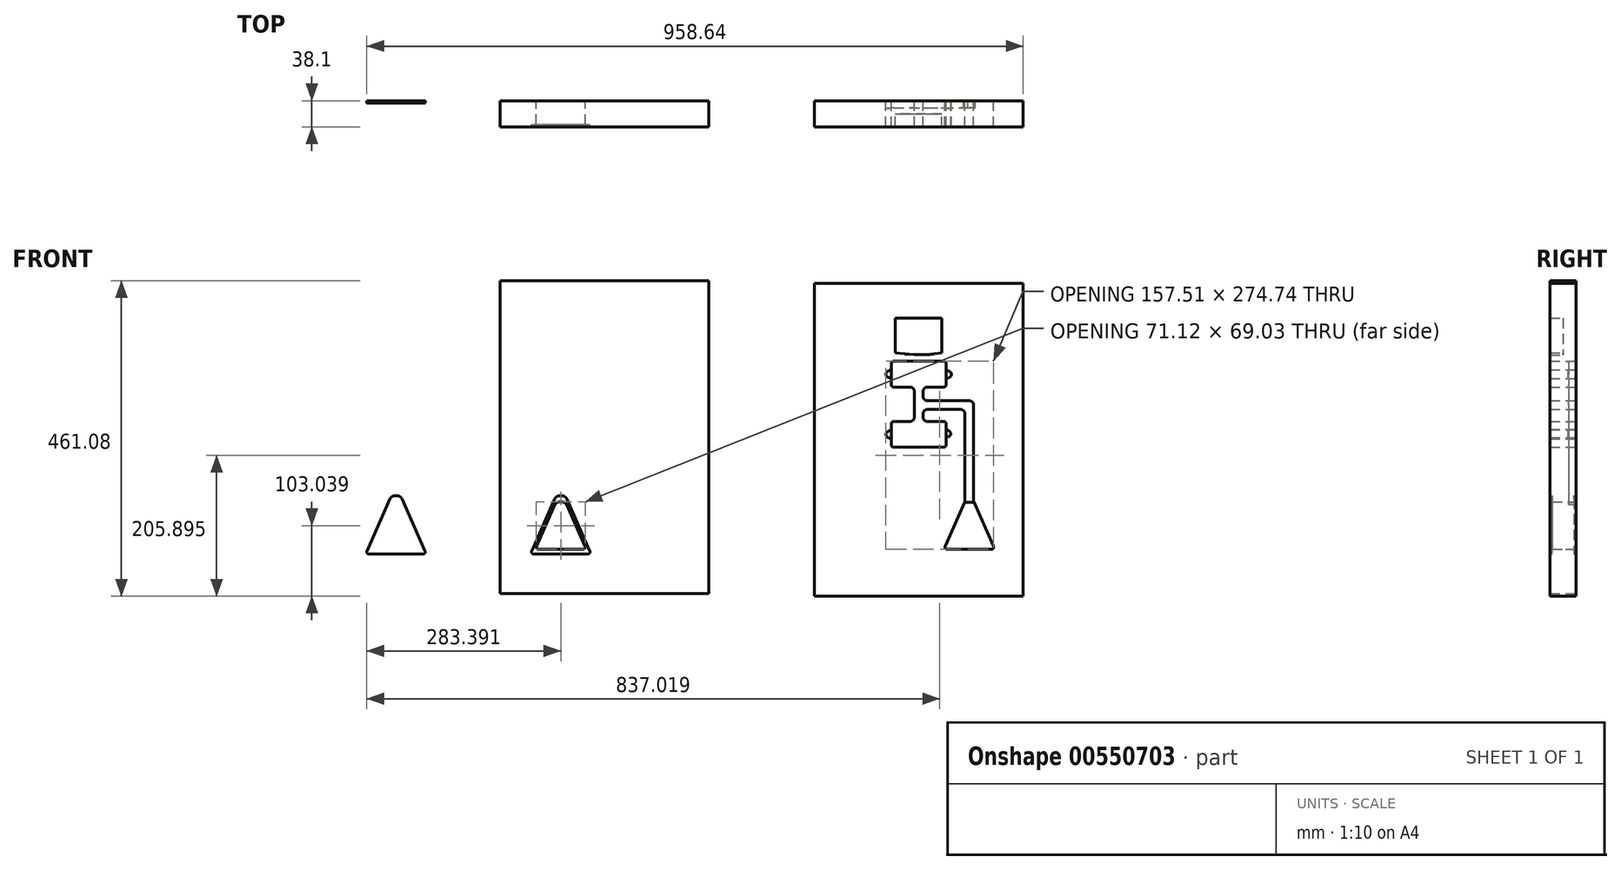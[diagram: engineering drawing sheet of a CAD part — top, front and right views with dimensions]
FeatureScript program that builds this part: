
annotation { "Feature Type Name" : "Feature", "Feature Type Description" : "" }
export const myFeature = defineFeature(function(context is Context, id is Id, definition is map)
    precondition{}
    {
        {
            var Q0;
            Q0=qCreatedBy(makeId("Front.planeOp"),FACE);
            var sketch = newSketch(context, id + "F0", { "sketchPlane" : qUnion([Q0])});
            skLineSegment(sketch, "E0.top", {"start": v(-152.36, -197.5) * mm, "end": v(152.44, -197.5) * mm});
            skLineSegment(sketch, "E0.left", {"start": v(-152.36, 208.9) * mm, "end": v(-152.36, -197.5) * mm});
            skLineSegment(sketch, "E0.right", {"start": v(152.44, 208.9) * mm, "end": v(152.44, -197.5) * mm});
            skLineSegment(sketch, "E1", {"start": v(-33.96, 208.9) * mm, "end": v(-33.96, 158.1) * mm});
            skLineSegment(sketch, "E2", {"start": v(34.04, 208.9) * mm, "end": v(34.04, 158.1) * mm});
            skLineSegment(sketch, "E3", {"start": v(0.04, 208.9) * mm, "end": v(0.04, -197.5) * mm, "construction": true});
            skLineSegment(sketch, "E4", {"start": v(-33.96, 158.1) * mm, "end": v(34.04, 158.1) * mm});
            skLineSegment(sketch, "E5.bottom", {"start": v(-36.8, 57.8) * mm, "end": v(-12.66, 57.8) * mm});
            skLineSegment(sketch, "E5.top", {"start": v(-36.8, 20.2) * mm, "end": v(36.87, 20.2) * mm});
            skLineSegment(sketch, "E5.left", {"start": v(-39.84, 54.75) * mm, "end": v(-39.84, 23.25) * mm});
            skLineSegment(sketch, "E5.right", {"start": v(39.92, 54.75) * mm, "end": v(39.92, 23.25) * mm});
            skLineSegment(sketch, "E6.bottom", {"start": v(-36.8, 145.75) * mm, "end": v(36.87, 145.75) * mm});
            skLineSegment(sketch, "E6.top", {"start": v(-36.8, 108.16) * mm, "end": v(-12.66, 108.16) * mm});
            skLineSegment(sketch, "E6.left", {"start": v(-39.84, 142.7) * mm, "end": v(-39.84, 111.2) * mm});
            skLineSegment(sketch, "E6.right", {"start": v(39.92, 142.7) * mm, "end": v(39.92, 111.2) * mm});
            skPoint(sketch, "E7.visualSharp", {"position": v(-39.84, 57.8) * mm});
            skArc(sketch, "E7.filletArc", {"start": v(-36.8, 57.8) * mm, "mid": v(-38.95, 56.9) * mm, "end": v(-39.84, 54.75) * mm});
            skPoint(sketch, "E8.visualSharp", {"position": v(39.92, 57.8) * mm});
            skArc(sketch, "E8.filletArc", {"start": v(39.92, 54.75) * mm, "mid": v(39.02, 56.9) * mm, "end": v(36.87, 57.8) * mm});
            skPoint(sketch, "E9.visualSharp", {"position": v(39.92, 20.2) * mm});
            skArc(sketch, "E9.filletArc", {"start": v(36.87, 20.2) * mm, "mid": v(39.02, 21.1) * mm, "end": v(39.92, 23.25) * mm});
            skPoint(sketch, "E10.visualSharp", {"position": v(-39.84, 20.2) * mm});
            skArc(sketch, "E10.filletArc", {"start": v(-39.84, 23.25) * mm, "mid": v(-38.95, 21.1) * mm, "end": v(-36.8, 20.2) * mm});
            skPoint(sketch, "E11.visualSharp", {"position": v(-39.84, 145.75) * mm});
            skArc(sketch, "E11.filletArc", {"start": v(-36.8, 145.75) * mm, "mid": v(-38.95, 144.86) * mm, "end": v(-39.84, 142.7) * mm});
            skPoint(sketch, "E12.visualSharp", {"position": v(39.92, 145.75) * mm});
            skArc(sketch, "E12.filletArc", {"start": v(39.92, 142.7) * mm, "mid": v(39.02, 144.86) * mm, "end": v(36.87, 145.75) * mm});
            skPoint(sketch, "E13.visualSharp", {"position": v(39.92, 108.16) * mm});
            skArc(sketch, "E13.filletArc", {"start": v(36.87, 108.16) * mm, "mid": v(39.02, 109.05) * mm, "end": v(39.92, 111.2) * mm});
            skPoint(sketch, "E14.visualSharp", {"position": v(-39.84, 108.16) * mm});
            skArc(sketch, "E14.filletArc", {"start": v(-39.84, 111.2) * mm, "mid": v(-38.95, 109.05) * mm, "end": v(-36.8, 108.16) * mm});
            skLineSegment(sketch, "E15", {"start": v(12.74, 88.05) * mm, "end": v(74.01, 88.05) * mm});
            skLineSegment(sketch, "E16", {"start": v(12.74, 75.35) * mm, "end": v(61.31, 75.35) * mm});
            skLineSegment(sketch, "E17", {"start": v(67.66, 69) * mm, "end": v(67.66, -58.67) * mm});
            skLineSegment(sketch, "E18", {"start": v(80.36, 81.7) * mm, "end": v(80.36, -58.67) * mm});
            skPoint(sketch, "E19.visualSharp", {"position": v(80.36, 88.05) * mm});
            skArc(sketch, "E19.filletArc", {"start": v(80.36, 81.7) * mm, "mid": v(78.5, 86.19) * mm, "end": v(74.01, 88.05) * mm});
            skPoint(sketch, "E20.visualSharp", {"position": v(67.66, 75.35) * mm});
            skArc(sketch, "E20.filletArc", {"start": v(67.66, 69) * mm, "mid": v(65.8, 73.49) * mm, "end": v(61.31, 75.35) * mm});
            skLineSegment(sketch, "E21", {"start": v(6.39, 101.81) * mm, "end": v(6.39, 94.4) * mm});
            skLineSegment(sketch, "E22", {"start": v(-6.31, 101.81) * mm, "end": v(-6.31, 64.15) * mm});
            skLineSegment(sketch, "E23.trimOffspring", {"start": v(6.39, 69) * mm, "end": v(6.39, 64.15) * mm});
            skLineSegment(sketch, "E24.trimOffspring", {"start": v(12.74, 108.16) * mm, "end": v(36.87, 108.16) * mm});
            skLineSegment(sketch, "E25.trimOffspring", {"start": v(12.74, 57.8) * mm, "end": v(36.87, 57.8) * mm});
            skPoint(sketch, "E26.visualSharp", {"position": v(6.39, 88.05) * mm});
            skArc(sketch, "E26.filletArc", {"start": v(6.39, 94.4) * mm, "mid": v(8.25, 89.9) * mm, "end": v(12.74, 88.05) * mm});
            skPoint(sketch, "E27.visualSharp", {"position": v(6.39, 108.16) * mm});
            skArc(sketch, "E27.filletArc", {"start": v(12.74, 108.16) * mm, "mid": v(8.25, 106.3) * mm, "end": v(6.39, 101.81) * mm});
            skPoint(sketch, "E28.visualSharp", {"position": v(-6.31, 108.16) * mm});
            skArc(sketch, "E28.filletArc", {"start": v(-6.31, 101.81) * mm, "mid": v(-8.17, 106.3) * mm, "end": v(-12.66, 108.16) * mm});
            skPoint(sketch, "E29.visualSharp", {"position": v(-6.31, 57.8) * mm});
            skArc(sketch, "E29.filletArc", {"start": v(-12.66, 57.8) * mm, "mid": v(-8.17, 59.66) * mm, "end": v(-6.31, 64.15) * mm});
            skPoint(sketch, "E30.visualSharp", {"position": v(6.39, 57.8) * mm});
            skArc(sketch, "E30.filletArc", {"start": v(6.39, 64.15) * mm, "mid": v(8.25, 59.66) * mm, "end": v(12.74, 57.8) * mm});
            skPoint(sketch, "E31.visualSharp", {"position": v(6.39, 75.35) * mm});
            skArc(sketch, "E31.filletArc", {"start": v(12.74, 75.35) * mm, "mid": v(8.25, 73.49) * mm, "end": v(6.39, 69) * mm});
            skLineSegment(sketch, "E32", {"start": v(34.04, 208.9) * mm, "end": v(-33.96, 208.9) * mm});
            skPoint(sketch, "E33.visualSharp", {"position": v(-152.36, 208.9) * mm});
            skLineSegment(sketch, "E34.bottom", {"start": v(-611.1, 263.57) * mm, "end": v(-306.3, 263.57) * mm});
            skLineSegment(sketch, "E34.top", {"start": v(-611.1, -193.63) * mm, "end": v(-306.3, -193.63) * mm});
            skLineSegment(sketch, "E34.left", {"start": v(-611.1, 263.57) * mm, "end": v(-611.1, -193.63) * mm});
            skLineSegment(sketch, "E34.right", {"start": v(-306.3, 263.57) * mm, "end": v(-306.3, -193.63) * mm});
            skLineSegment(sketch, "E35", {"start": v(-39.84, 133.56) * mm, "end": v(-45.04, 131.3) * mm});
            skLineSegment(sketch, "E36", {"start": v(-44.9, 122.39) * mm, "end": v(-39.84, 120.35) * mm});
            skLineSegment(sketch, "E37", {"start": v(39.92, 133.56) * mm, "end": v(45.31, 130.87) * mm});
            skLineSegment(sketch, "E38", {"start": v(44.71, 121.98) * mm, "end": v(39.92, 120.35) * mm});
            skLineSegment(sketch, "E39", {"start": v(-39.84, 45.6) * mm, "end": v(-44.97, 43.45) * mm});
            skPoint(sketch, "E39.endSnap0", {"position": v(-39.84, 39) * mm});
            skLineSegment(sketch, "E40", {"start": v(-44.97, 34.55) * mm, "end": v(-39.84, 32.4) * mm});
            skPoint(sketch, "E41.endSnap0", {"position": v(39.92, 39) * mm});
            skPoint(sketch, "E42.visualSharp", {"position": v(-55.59, 39) * mm});
            skArc(sketch, "E42.filletArc", {"start": v(-44.97, 43.45) * mm, "mid": v(-47.93, 39) * mm, "end": v(-44.97, 34.55) * mm});
            skLineSegment(sketch, "E43.filletArc", {"start": v(53.74, 35.22) * mm, "end": v(53.74, 35.22) * mm});
            skPoint(sketch, "E44.visualSharp", {"position": v(55.66, 125.7) * mm});
            skArc(sketch, "E44.filletArc", {"start": v(44.71, 121.98) * mm, "mid": v(47.97, 126.23) * mm, "end": v(45.31, 130.87) * mm});
            skPoint(sketch, "E45.visualSharp", {"position": v(-55.59, 126.68) * mm});
            skArc(sketch, "E45.filletArc", {"start": v(-45.04, 131.3) * mm, "mid": v(-47.93, 126.8) * mm, "end": v(-44.9, 122.39) * mm});
            skLineSegment(sketch, "E46", {"start": v(39.92, 46.1) * mm, "end": v(43.96, 44.28) * mm});
            skLineSegment(sketch, "E47", {"start": v(43.38, 35.27) * mm, "end": v(39.92, 34.22) * mm});
            skPoint(sketch, "E48.visualSharp", {"position": v(55.66, 39) * mm});
            skArc(sketch, "E48.filletArc", {"start": v(43.38, 35.27) * mm, "mid": v(46.8, 39.57) * mm, "end": v(43.96, 44.28) * mm});
            skLineSegment(sketch, "E49", {"start": v(0.04, 158.1) * mm, "end": v(0.04, 155.1) * mm});
            skLineSegment(sketch, "E50", {"start": v(-33.96, 158.1) * mm, "end": v(-20.85, 156.56) * mm});
            skLineSegment(sketch, "E51", {"start": v(-13.84, 155.94) * mm, "end": v(-6.36, 155.48) * mm});
            skLineSegment(sketch, "E52", {"start": v(11.08, 155.53) * mm, "end": v(6.44, 155.35) * mm});
            skLineSegment(sketch, "E53", {"start": v(23.33, 156.62) * mm, "end": v(34.04, 158.1) * mm});
            skPoint(sketch, "E54.visualSharp", {"position": v(-17.36, 156.15) * mm});
            skArc(sketch, "E54.filletArc", {"start": v(-20.85, 156.56) * mm, "mid": v(-17.35, 156.2) * mm, "end": v(-13.84, 155.94) * mm});
            skPoint(sketch, "E55.visualSharp", {"position": v(17.23, 155.78) * mm});
            skArc(sketch, "E55.filletArc", {"start": v(11.08, 155.53) * mm, "mid": v(17.21, 155.93) * mm, "end": v(23.33, 156.62) * mm});
            skPoint(sketch, "E56.visualSharp", {"position": v(0.04, 155.1) * mm});
            skArc(sketch, "E56.filletArc", {"start": v(-6.36, 155.48) * mm, "mid": v(0.04, 155.25) * mm, "end": v(6.44, 155.35) * mm});
            skLineSegment(sketch, "E57", {"start": v(65.67, -63.82) * mm, "end": v(38.72, -124.52) * mm});
            skLineSegment(sketch, "E58", {"start": v(82.35, -63.82) * mm, "end": v(109.3, -124.52) * mm});
            skLineSegment(sketch, "E59", {"start": v(41.62, -128.98) * mm, "end": v(106.4, -128.98) * mm});
            skPoint(sketch, "E60.visualSharp", {"position": v(36.73, -128.98) * mm});
            skArc(sketch, "E60.filletArc", {"start": v(38.72, -124.52) * mm, "mid": v(38.96, -127.54) * mm, "end": v(41.62, -128.98) * mm});
            skPoint(sketch, "E61.visualSharp", {"position": v(111.3, -128.98) * mm});
            skArc(sketch, "E61.filletArc", {"start": v(106.4, -128.98) * mm, "mid": v(109.07, -127.54) * mm, "end": v(109.3, -124.52) * mm});
            skPoint(sketch, "E62.visualSharp", {"position": v(80.36, -59.34) * mm});
            skArc(sketch, "E62.filletArc", {"start": v(80.36, -58.67) * mm, "mid": v(80.43, -59.33) * mm, "end": v(80.64, -59.96) * mm});
            skPoint(sketch, "E63.visualSharp", {"position": v(67.66, -59.34) * mm});
            skArc(sketch, "E63.filletArc", {"start": v(67.4, -59.96) * mm, "mid": v(67.6, -59.33) * mm, "end": v(67.66, -58.67) * mm});
            skLineSegment(sketch, "E64.MirrorCS", {"start": v(-514.51, -63.73) * mm, "end": v(-487.51, -124.52) * mm});
            skLineSegment(sketch, "E65.MirrorCS", {"start": v(-531.1, -63.73) * mm, "end": v(-558.1, -124.52) * mm});
            skArc(sketch, "E66.MirrorCS", {"start": v(-555.2, -128.98) * mm, "mid": v(-557.87, -127.54) * mm, "end": v(-558.1, -124.52) * mm});
            skLineSegment(sketch, "E67.MirrorCS", {"start": v(-490.41, -128.98) * mm, "end": v(-555.2, -128.98) * mm});
            skArc(sketch, "E68.MirrorCS", {"start": v(-487.51, -124.52) * mm, "mid": v(-487.75, -127.54) * mm, "end": v(-490.41, -128.98) * mm});
            skLineSegment(sketch, "E69", {"start": v(-525.3, -59.96) * mm, "end": v(-520.31, -59.96) * mm});
            skPoint(sketch, "E70.visualSharp", {"position": v(-529.43, -59.96) * mm});
            skArc(sketch, "E70.filletArc", {"start": v(-525.3, -59.96) * mm, "mid": v(-528.77, -60.98) * mm, "end": v(-531.1, -63.73) * mm});
            skPoint(sketch, "E71.visualSharp", {"position": v(-516.19, -59.96) * mm});
            skArc(sketch, "E71.filletArc", {"start": v(-514.51, -63.73) * mm, "mid": v(-516.85, -60.98) * mm, "end": v(-520.31, -59.96) * mm});
            skLineSegment(sketch, "E72", {"start": v(-525.3, -50.88) * mm, "end": v(-520.31, -50.88) * mm});
            skLineSegment(sketch, "E73", {"start": v(-514.51, -54.65) * mm, "end": v(-480.36, -131.55) * mm});
            skLineSegment(sketch, "E74", {"start": v(-483.26, -136.01) * mm, "end": v(-562.36, -136.01) * mm});
            skLineSegment(sketch, "E75", {"start": v(-565.26, -131.55) * mm, "end": v(-531.1, -54.65) * mm});
            skPoint(sketch, "E76.visualSharp", {"position": v(-529.43, -50.88) * mm});
            skArc(sketch, "E76.filletArc", {"start": v(-525.3, -50.88) * mm, "mid": v(-528.77, -51.9) * mm, "end": v(-531.1, -54.65) * mm});
            skPoint(sketch, "E77.visualSharp", {"position": v(-516.19, -50.88) * mm});
            skArc(sketch, "E77.filletArc", {"start": v(-514.51, -54.65) * mm, "mid": v(-516.85, -51.9) * mm, "end": v(-520.31, -50.88) * mm});
            skPoint(sketch, "E78.visualSharp", {"position": v(-567.24, -136.01) * mm});
            skArc(sketch, "E78.filletArc", {"start": v(-565.26, -131.55) * mm, "mid": v(-565.02, -134.57) * mm, "end": v(-562.36, -136.01) * mm});
            skPoint(sketch, "E79.visualSharp", {"position": v(-478.38, -136.01) * mm});
            skArc(sketch, "E79.filletArc", {"start": v(-483.26, -136.01) * mm, "mid": v(-480.6, -134.57) * mm, "end": v(-480.36, -131.55) * mm});
            skLineSegment(sketch, "E80", {"start": v(-531.1, -54.65) * mm, "end": v(-565.26, -131.55) * mm});
            skLineSegment(sketch, "E81.MirrorCS", {"start": v(-755.18, -54.65) * mm, "end": v(-721.03, -131.55) * mm});
            skLineSegment(sketch, "E82.MirrorCS", {"start": v(-803.03, -136.01) * mm, "end": v(-723.93, -136.01) * mm});
            skLineSegment(sketch, "E83.MirrorCS", {"start": v(-771.78, -54.65) * mm, "end": v(-805.93, -131.55) * mm});
            skArc(sketch, "E84.MirrorCS", {"start": v(-771.78, -54.65) * mm, "mid": v(-769.44, -51.9) * mm, "end": v(-765.98, -50.88) * mm});
            skLineSegment(sketch, "E85.MirrorCS", {"start": v(-760.99, -50.88) * mm, "end": v(-765.98, -50.88) * mm});
            skArc(sketch, "E86.MirrorCS", {"start": v(-760.99, -50.88) * mm, "mid": v(-757.52, -51.9) * mm, "end": v(-755.18, -54.65) * mm});
            skArc(sketch, "E87.MirrorCS", {"start": v(-721.03, -131.55) * mm, "mid": v(-721.27, -134.57) * mm, "end": v(-723.93, -136.01) * mm});
            skArc(sketch, "E88.MirrorCS", {"start": v(-803.03, -136.01) * mm, "mid": v(-805.69, -134.57) * mm, "end": v(-805.93, -131.55) * mm});
            skLineSegment(sketch, "E89", {"start": v(-41.46, 1.36) * mm, "end": v(41.54, 1.36) * mm});
            skLineSegment(sketch, "E90.MirrorCS", {"start": v(-892.24, -63.73) * mm, "end": v(-865.24, -124.52) * mm});
            skArc(sketch, "E91.MirrorCS", {"start": v(-868.15, -128.98) * mm, "mid": v(-865.48, -127.54) * mm, "end": v(-865.24, -124.52) * mm});
            skLineSegment(sketch, "E92.MirrorCS", {"start": v(-932.93, -128.98) * mm, "end": v(-868.15, -128.98) * mm});
            skArc(sketch, "E93.MirrorCS", {"start": v(-936.02, -124.52) * mm, "mid": v(-935.78, -127.54) * mm, "end": v(-933.12, -128.98) * mm});
            skLineSegment(sketch, "E94.MirrorCS", {"start": v(-908.84, -63.73) * mm, "end": v(-935.84, -124.52) * mm});
            skArc(sketch, "E95.MirrorCS", {"start": v(-908.37, -66.5) * mm, "mid": v(-906.03, -63.75) * mm, "end": v(-902.57, -62.72) * mm});
            skLineSegment(sketch, "E96.MirrorCS", {"start": v(-897.58, -62.72) * mm, "end": v(-902.57, -62.72) * mm});
            skArc(sketch, "E97.MirrorCS", {"start": v(-897.58, -62.72) * mm, "mid": v(-894.09, -63.69) * mm, "end": v(-891.7, -66.4) * mm});
            skPoint(sketch, "E98.endSnap0", {"position": v(109.07, -127.54) * mm});
            skPoint(sketch, "E99.endSnap0", {"position": v(-935.78, -127.54) * mm});
            skArc(sketch, "E100.MirrorCS", {"start": v(71.54, -60.1) * mm, "mid": v(68.05, -61.1) * mm, "end": v(65.67, -63.82) * mm});
            skLineSegment(sketch, "E101.MirrorCS", {"start": v(71.54, -60.1) * mm, "end": v(76.53, -60.08) * mm});
            skArc(sketch, "E102.MirrorCS", {"start": v(82.35, -63.82) * mm, "mid": v(80, -61.09) * mm, "end": v(76.53, -60.08) * mm});
            skPoint(sketch, "E103.start.orphan", {"position": v(65.67, -63.82) * mm});
            skPoint(sketch, "E104.start.orphan", {"position": v(82.35, -63.82) * mm});
            skLineSegment(sketch, "E105", {"start": v(67.4, -59.96) * mm, "end": v(65.67, -63.82) * mm});
            skLineSegment(sketch, "E106", {"start": v(80.64, -59.96) * mm, "end": v(82.35, -63.82) * mm});
            skLineSegment(sketch, "E107", {"start": v(-55.59, -128.98) * mm, "end": v(-55.59, 126.68) * mm, "construction": true});
            skLineSegment(sketch, "E108", {"start": v(-55.59, -128.98) * mm, "end": v(111.3, -128.98) * mm, "construction": true});
            skLineSegment(sketch, "E109", {"start": v(-55.59, -128.98) * mm, "end": v(-55.59, 208.9) * mm, "construction": true});
            skLineSegment(sketch, "E110", {"start": v(55.66, 125.7) * mm, "end": v(55.66, 39) * mm, "construction": true});
            skLineSegment(sketch, "E111.bottom", {"start": v(-33.96, 208.9) * mm, "end": v(34.04, 208.9) * mm});
            skLineSegment(sketch, "E111.top", {"start": v(-152.36, 259.7) * mm, "end": v(152.44, 259.7) * mm});
            skLineSegment(sketch, "E111.left", {"start": v(-152.36, 208.9) * mm, "end": v(-152.36, 259.7) * mm});
            skLineSegment(sketch, "E111.right", {"start": v(152.44, 208.9) * mm, "end": v(152.44, 259.7) * mm});
            skSolve(sketch);
        }
        {
            var Q0;
            Q0=makeQuery(id+"F0.imprint","IMPRINT",FACE,{"disambiguationData":[TD([[makeQuery(id+"F0.imprint","IMPRINT",EDGE,{"derivedFrom":sQuery(id+"F0.wireOp",EDGE,"E1")}),-1.0]])]});
            var Q1;
            Q1=makeQuery(id+"F0.imprint","IMPRINT",FACE,{"disambiguationData":[TD([[makeQuery(id+"F0.imprint","IMPRINT",EDGE,{"derivedFrom":sQuery(id+"F0.wireOp",EDGE,"E34.bottom")}),-1.0]])]});
            extrude(context, id + "F1", {"entities" : qUnion([Q0, Q1]), "depth" : 38.1 * mm, "offsetDistance" : 25.4 * mm});
        }
        {
            var Q0;
            Q0=makeQuery(id+"F0.imprint","IMPRINT",FACE,{"disambiguationData":[TD([[makeQuery(id+"F0.imprint","IMPRINT",EDGE,{"derivedFrom":sQuery(id+"F0.wireOp",EDGE,"E5.bottom")}),-1.0]])]});
            var Q1;
            Q1=makeQuery(id+"F0.imprint","IMPRINT",FACE,{"disambiguationData":[TD([[makeQuery(id+"F0.imprint","IMPRINT",EDGE,{"derivedFrom":sQuery(id+"F0.wireOp",EDGE,"ct9IZTCw-5HtW-eV2D-LJwn-MinTb3ySNKOT")}),-1.0]])]});
            var Q2;
            {var subQ1=sQuery(id+"F0.wireOp",EDGE,"E62.filletArc");Q2=makeQuery(id+"F0.imprint","IMPRINT",FACE,{"disambiguationData":[TD([[makeQuery(id+"F0.imprint","IMPRINT",EDGE,{"derivedFrom":subQ1}),-1.0]])]});}
            extrude(context, id + "F2", {"entities" : qUnion([Q0, Q1, Q2]), "depth" : 10.38 * mm, "offsetDistance" : 25.4 * mm});
        }
        {
            var Q0;
            {var subQ0=sQuery(id+"F0.wireOp",EDGE,"E35");Q0=makeQuery(id+"F0.imprint","IMPRINT",FACE,{"disambiguationData":[TD([[makeQuery(id+"F0.imprint","IMPRINT",EDGE,{"derivedFrom":subQ0}),1.0]])]});}
            var Q1;
            {var subQ0=sQuery(id+"F0.wireOp",EDGE,"E37");Q1=makeQuery(id+"F0.imprint","IMPRINT",FACE,{"disambiguationData":[TD([[makeQuery(id+"F0.imprint","IMPRINT",EDGE,{"derivedFrom":subQ0}),-1.0]])]});}
            var Q2;
            {var subQ0=sQuery(id+"F0.wireOp",EDGE,"E41");Q2=makeQuery(id+"F0.imprint","IMPRINT",FACE,{"disambiguationData":[TD([[makeQuery(id+"F0.imprint","IMPRINT",EDGE,{"derivedFrom":subQ0}),-1.0]])]});}
            var Q3;
            {var subQ0=sQuery(id+"F0.wireOp",EDGE,"E39");Q3=makeQuery(id+"F0.imprint","IMPRINT",FACE,{"disambiguationData":[TD([[makeQuery(id+"F0.imprint","IMPRINT",EDGE,{"derivedFrom":subQ0}),1.0]])]});}
            var Q4;
            {var subQ0=sQuery(id+"F0.wireOp",EDGE,"E46");Q4=makeQuery(id+"F0.imprint","IMPRINT",FACE,{"disambiguationData":[TD([[makeQuery(id+"F0.imprint","IMPRINT",EDGE,{"derivedFrom":subQ0}),-1.0]])]});}
            extrude(context, id + "F3", {"entities" : qUnion([Q0, Q1, Q2, Q3, Q4]), "depth" : 10.9 * mm, "offsetDistance" : 25.4 * mm});
        }
        {
            var Q0;
            Q0=makeQuery(id+"F0.imprint","IMPRINT",FACE,{"disambiguationData":[TD([[makeQuery(id+"F0.imprint","IMPRINT",EDGE,{"derivedFrom":sQuery(id+"F0.wireOp",EDGE,"E1")}),1.0]])]});
            var Q1;
            {var subQ1=sQuery(id+"F0.wireOp",EDGE,"E50");Q1=makeQuery(id+"F0.imprint","IMPRINT",FACE,{"disambiguationData":[TD([[makeQuery(id+"F0.imprint","IMPRINT",EDGE,{"derivedFrom":subQ1}),1.0]])]});}
            var Q2;
            {var subQ1=sQuery(id+"F0.wireOp",EDGE,"E52");Q2=makeQuery(id+"F0.imprint","IMPRINT",FACE,{"disambiguationData":[TD([[makeQuery(id+"F0.imprint","IMPRINT",EDGE,{"derivedFrom":subQ1}),-1.0]])]});}
            extrude(context, id + "F4", {"entities" : qUnion([Q0, Q1, Q2]), "operationType" : NewBodyOperationType.ADD, "depth" : 19.05 * mm, "offsetDistance" : 25.4 * mm});
        }
        {
            var Q0;
            Q0=makeQuery(id+"F0.imprint","IMPRINT",FACE,{"disambiguationData":[TD([[makeQuery(id+"F0.imprint","IMPRINT",EDGE,{"derivedFrom":sQuery(id+"F0.wireOp",EDGE,"E64.MirrorCS")}),1.0]])]});
            extrude(context, id + "F5", {"entities" : qUnion([Q0]), "operationType" : NewBodyOperationType.ADD, "depth" : 34.92 * mm, "offsetDistance" : 25.4 * mm});
        }
        {
            var Q0;
            Q0=makeQuery(id+"F0.imprint","IMPRINT",FACE,{"disambiguationData":[TD([[makeQuery(id+"F0.imprint","IMPRINT",EDGE,{"derivedFrom":sQuery(id+"F0.wireOp",EDGE,"E81.MirrorCS")}),-1.0]])]});
            extrude(context, id + "F6", {"entities" : qUnion([Q0]), "depth" : 3.17 * mm, "offsetDistance" : 25.4 * mm});
        }
    });
